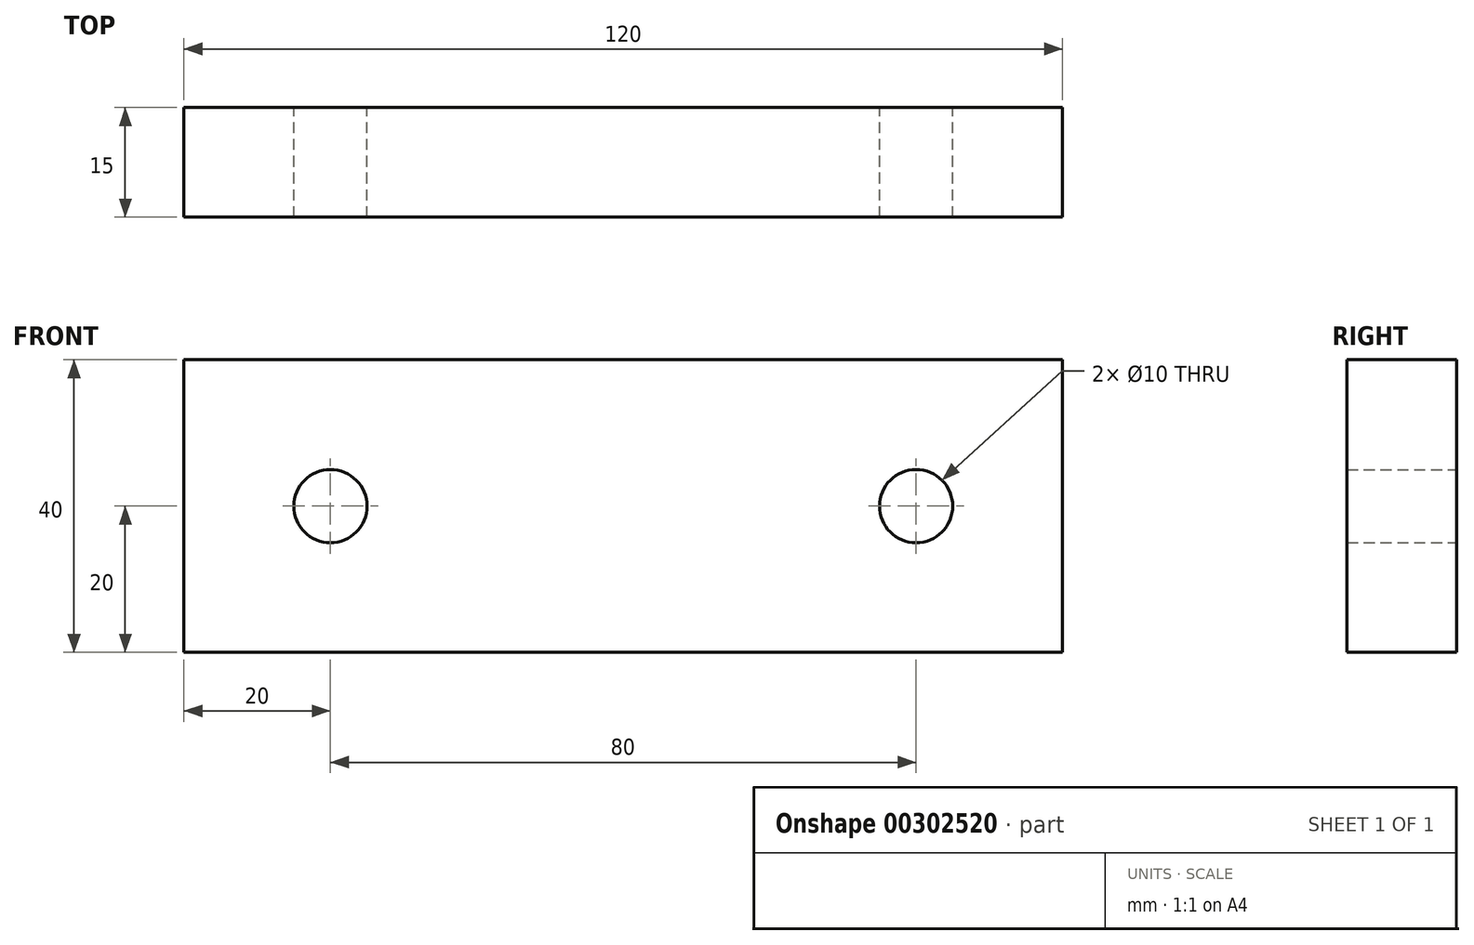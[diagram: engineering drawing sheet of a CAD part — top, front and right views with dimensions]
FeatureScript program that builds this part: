
annotation { "Feature Type Name" : "Feature", "Feature Type Description" : "" }
export const myFeature = defineFeature(function(context is Context, id is Id, definition is map)
    precondition{}
    {
        {
            var Q0;
            Q0=qCreatedBy(makeId("Front.planeOp"),FACE);
            var sketch = newSketch(context, id + "F0", { "sketchPlane" : qUnion([Q0])});
            skLineSegment(sketch, "E0.bottom", {"start": v(0, 0) * mm, "end": v(120, 0) * mm});
            skLineSegment(sketch, "E0.top", {"start": v(0, 40) * mm, "end": v(120, 40) * mm});
            skLineSegment(sketch, "E0.left", {"start": v(0, 0) * mm, "end": v(0, 40) * mm});
            skLineSegment(sketch, "E0.right", {"start": v(120, 0) * mm, "end": v(120, 40) * mm});
            skCircle(sketch, "E1", {"center": v(20, 20) * mm, "radius": 5 * mm});
            skCircle(sketch, "E2", {"center": v(100, 20) * mm, "radius": 5 * mm});
            skSolve(sketch);
        }
        {
            var Q0;
            Q0=makeQuery(id+"F0.imprint","IMPRINT",FACE,{"disambiguationData":[TD([[makeQuery(id+"F0.imprint","IMPRINT",EDGE,{"derivedFrom":sQuery(id+"F0.wireOp",EDGE,"E0.bottom")}),1.0]])]});
            extrude(context, id + "F1", {"entities" : qUnion([Q0]), "depth" : 15 * mm});
        }
    });
